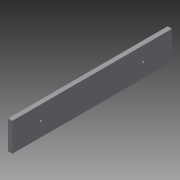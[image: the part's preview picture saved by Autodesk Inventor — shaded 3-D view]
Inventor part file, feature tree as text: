
AUTODESK INVENTOR PART (.ipt)
format: ipt  version: 2015 SP1 (Build 190203100, 203)  size: 82,944 bytes
history: native  units: in
note: dims shown in document units (in); Inventor stores cm internally (conversion verified against a paired STEP export)
features: sketch x2, extrude x1, hole x1, projected_geometry x1
ambient origin geometry x8: Origin, YZ Plane, XZ Plane, XY Plane, X Axis, Y Axis, Z Axis, Center Point
bodies: Solid1 (feature_tree)
feature tree (5):
  extrude  "Extrusion1"  Depth=5.0in
  hole  "Hole1"  [1 undecoded]
  sketch  "Sketch1"  dims[d0=0.75in d1=5.0in]
  sketch  "Sketch4"  dims[d2=28.0in d3=0.0in d18=2.5in d19=2.5in d20=5.0in d21=5.0in d22=0.3125in d23=0.75in d24=0.375in d25=0.25in d26=0.5635in d27=1.0in d28=0.8108in]
  projected_geometry  "Projected Loop3"
note: 1 required parameter value undecoded (feature->parameter linkage not recoverable at this tier; creation-order binding heuristic only, values carry confidence <= 0.55)
